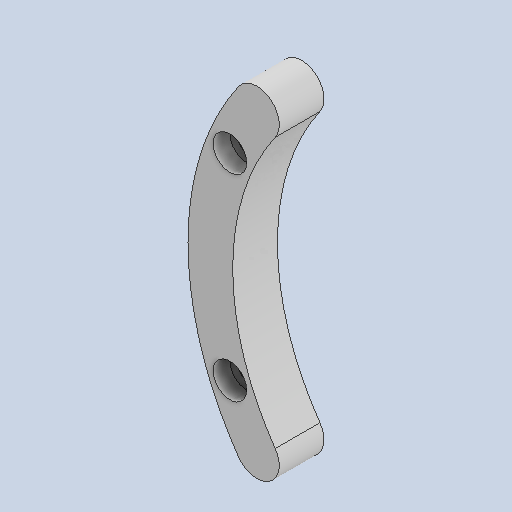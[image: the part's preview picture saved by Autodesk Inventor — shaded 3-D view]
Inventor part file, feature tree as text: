
AUTODESK INVENTOR PART (.ipt)
format: ipt  version: 2024.3 (Build 283343000, 343)  size: 130,560 bytes
history: native  units: mm
features: extrude x2, sketch x2, other x1, fillet x1
ambient origin geometry x8: Origin, YZ Plane, XZ Plane, XY Plane, X Axis, Y Axis, Z Axis, Center Point
bodies: Body1 (feature_tree)
feature tree (6):
  other  "ソリッド1"
  extrude  "押し出し1"  Depth=92.0mm
  fillet  "フィレット1"  Radius=100.0mm
  extrude  "押し出し2"  Depth=84.0mm
  sketch  "スケッチ1"
  sketch  "スケッチ2"
